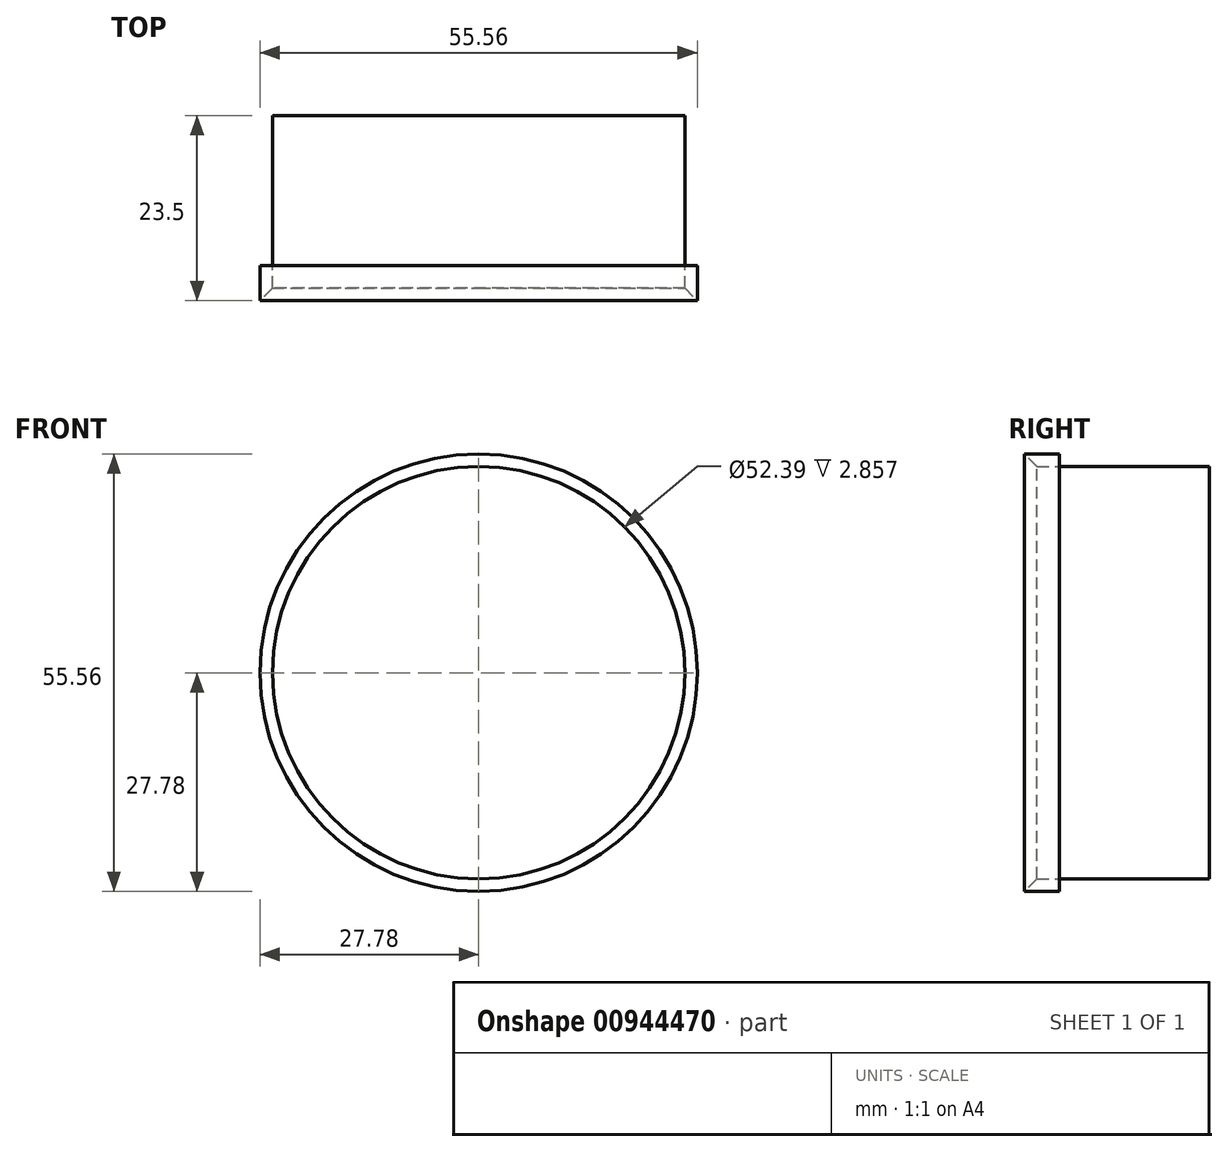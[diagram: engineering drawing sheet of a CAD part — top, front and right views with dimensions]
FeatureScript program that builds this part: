
annotation { "Feature Type Name" : "Feature", "Feature Type Description" : "" }
export const myFeature = defineFeature(function(context is Context, id is Id, definition is map)
    precondition{}
    {
        {
            var Q0;
            Q0=qCreatedBy(makeId("Front.planeOp"),FACE);
            var sketch = newSketch(context, id + "F0", { "sketchPlane" : qUnion([Q0])});
            skCircle(sketch, "E0", {"center": v(0, 0) * mm, "radius": 26.2 * mm});
            skSolve(sketch);
        }
        {
            var Q0;
            Q0=makeQuery(id+"F0.imprint","IMPRINT",FACE,{"disambiguationData":[TD([[makeQuery(id+"F0.imprint","IMPRINT",EDGE,{"derivedFrom":sQuery(id+"F0.wireOp",EDGE,"E0")}),1.0]])]});
            extrude(context, id + "F1", {"entities" : qUnion([Q0]), "depth" : 19.05 * mm, "offsetDistance" : 25.4 * mm});
        }
        {
            var Q0;
            Q0=makeQuery(id+"F1.opExtrude","CAP_FACE",FACE,{"disambiguationData":[OSD([sQuery(id+"F0.wireOp",EDGE,"E0")])],"isStart":false});
            var sketch = newSketch(context, id + "F2", { "sketchPlane" : qUnion([Q0])});
            skCircle(sketch, "E1", {"center": v(0, 0) * mm, "radius": 27.78 * mm});
            skSolve(sketch);
        }
        {
            var Q0;
            Q0=makeQuery(id+"F2.imprint","IMPRINT",FACE,{"disambiguationData":[TD([[makeQuery(id+"F2.imprint","IMPRINT",EDGE,{"derivedFrom":sQuery(id+"F2.wireOp",EDGE,"E1")}),1.0]])]});
            extrude(context, id + "F3", {"entities" : qUnion([Q0]), "depth" : 7.94 * mm, "offsetDistance" : 25.4 * mm});
        }
        {
            var Q0;
            Q0=makeQuery(id+"F3.opExtrude","CAP_EDGE",EDGE,{"disambiguationData":[OSD([sQuery(id+"F0.wireOp",EDGE,"E0")])],"isStart":false});
            chamfer(context, id + "F4", {"entities" : qUnion([Q0]), "width" : 5.08 * mm, "tangentPropagation" : true});
        }
    });
